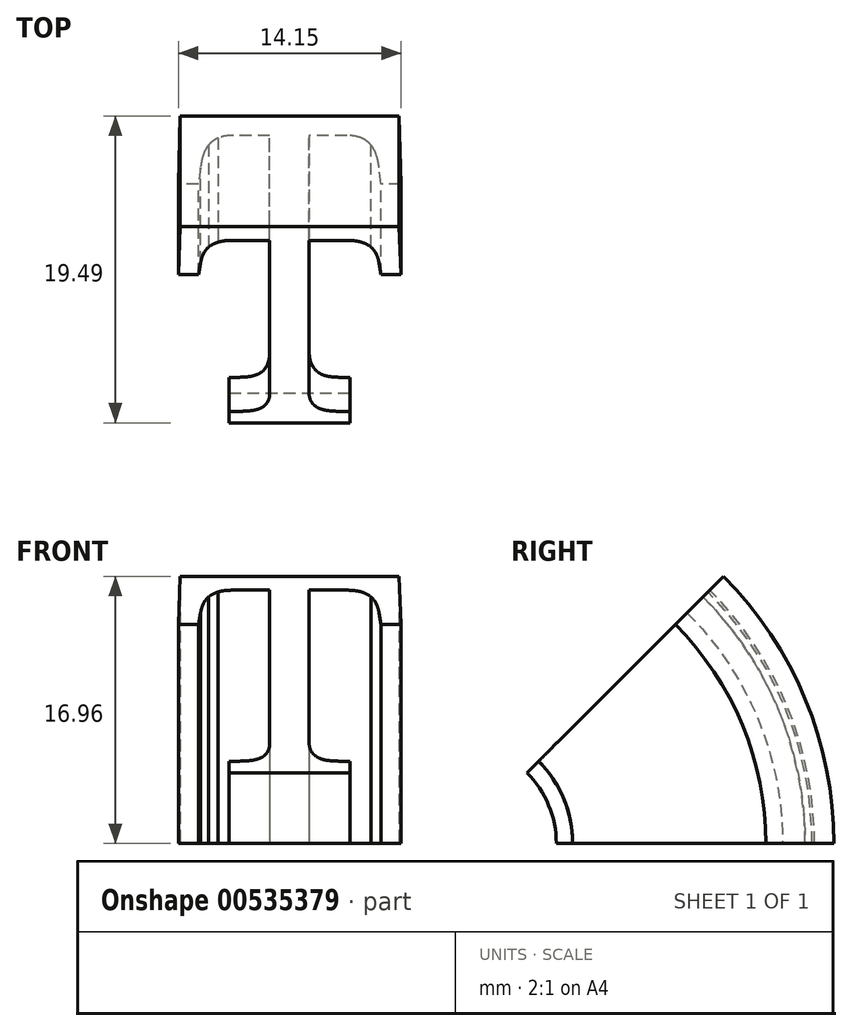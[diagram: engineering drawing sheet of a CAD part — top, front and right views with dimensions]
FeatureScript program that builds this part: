
annotation { "Feature Type Name" : "Feature", "Feature Type Description" : "" }
export const myFeature = defineFeature(function(context is Context, id is Id, definition is map)
    precondition{}
    {
        {
            var Q0;
            Q0=qCreatedBy(makeId("Top.planeOp"),FACE);
            var sketch = newSketch(context, id + "F0", { "sketchPlane" : qUnion([Q0])});
            skText(sketch, "E0", { "text": "T", "fontName": "NotoSerif-Regular.ttf"});
            skLineSegment(sketch, "E1", {"start": v(-8.12, 0) * mm, "end": v(-8.12, -6.35) * mm});
            skLineSegment(sketch, "E2", {"start": v(-8.12, -6.35) * mm, "end": v(8.5, -6.35) * mm});
            const initialGuessF0  = {"E0": [-0.00812, 0, 1, 0, 0.01778]};
            skSetInitialGuess(sketch, initialGuessF0);
            skSolve(sketch);
        }
        {
            var Q0;
            Q0 = qSketchRegion(id + "F0", true);
            var Q1;
            Q1=sQuery(id+"F0.wireOp",EDGE,"E2");
            revolve(context, id + "F1", {"entities" : qUnion([Q0]), "axis" : qUnion([Q1]), "revolveType" : RevolveType.ONE_DIRECTION, "angle" : 45 * degree});
        }
    });
